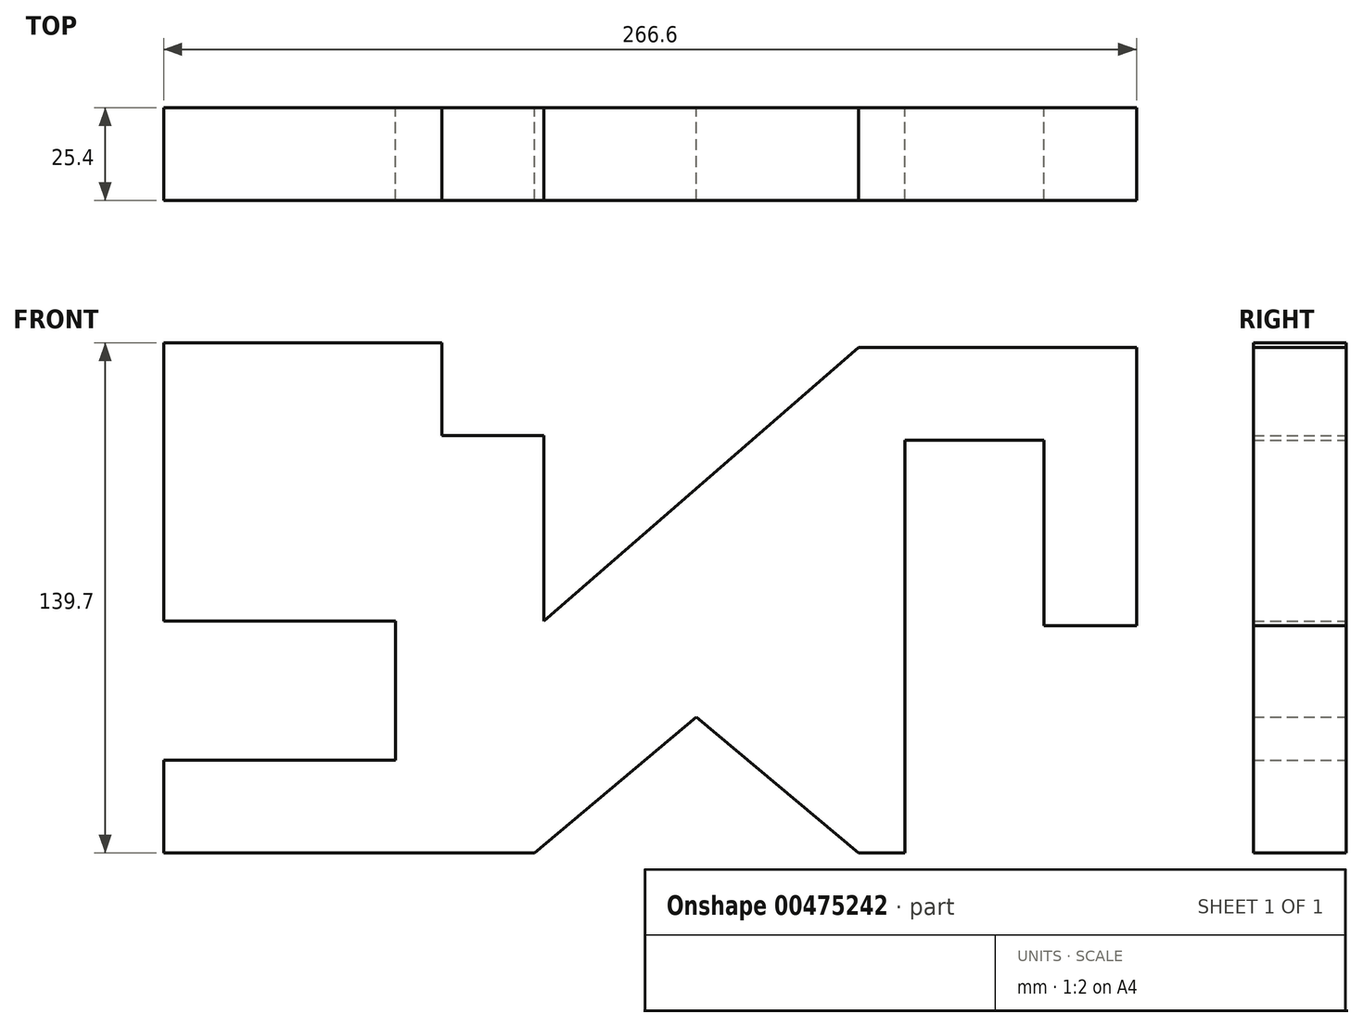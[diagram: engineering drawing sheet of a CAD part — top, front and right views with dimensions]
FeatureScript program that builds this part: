
annotation { "Feature Type Name" : "Feature", "Feature Type Description" : "" }
export const myFeature = defineFeature(function(context is Context, id is Id, definition is map)
    precondition{}
    {
        {
            var Q0;
            Q0=qCreatedBy(makeId("Front.planeOp"),FACE);
            var sketch = newSketch(context, id + "F0", { "sketchPlane" : qUnion([Q0])});
            skLineSegment(sketch, "E0", {"start": v(0, 0) * mm, "end": v(0, 76.2) * mm});
            skLineSegment(sketch, "E1", {"start": v(0, 76.2) * mm, "end": v(76.2, 76.2) * mm});
            skLineSegment(sketch, "E2", {"start": v(76.2, 76.2) * mm, "end": v(76.2, 50.8) * mm});
            skLineSegment(sketch, "E3", {"start": v(76.2, 50.8) * mm, "end": v(104.14, 50.8) * mm});
            skLineSegment(sketch, "E4", {"start": v(104.14, 50.8) * mm, "end": v(104.14, 0) * mm});
            skLineSegment(sketch, "E5", {"start": v(104.14, 0) * mm, "end": v(190.4, 74.99) * mm});
            skLineSegment(sketch, "E6", {"start": v(0, 0) * mm, "end": v(63.5, 0) * mm});
            skLineSegment(sketch, "E7", {"start": v(63.5, 0) * mm, "end": v(63.5, -38.1) * mm});
            skLineSegment(sketch, "E8", {"start": v(63.5, -38.1) * mm, "end": v(0, -38.1) * mm});
            skLineSegment(sketch, "E9", {"start": v(0, -38.1) * mm, "end": v(0, -63.5) * mm});
            skLineSegment(sketch, "E10", {"start": v(0, -63.5) * mm, "end": v(101.6, -63.5) * mm});
            skLineSegment(sketch, "E11", {"start": v(101.6, -63.5) * mm, "end": v(146, -26.24) * mm});
            skLineSegment(sketch, "E12", {"start": v(146, -26.24) * mm, "end": v(190.4, -63.5) * mm});
            skLineSegment(sketch, "E13", {"start": v(190.4, -63.5) * mm, "end": v(203.1, -63.5) * mm});
            skLineSegment(sketch, "E14", {"start": v(190.4, 74.99) * mm, "end": v(266.6, 74.99) * mm});
            skLineSegment(sketch, "E15", {"start": v(266.6, 74.99) * mm, "end": v(266.6, -1.21) * mm});
            skLineSegment(sketch, "E16", {"start": v(266.6, -1.21) * mm, "end": v(241.2, -1.21) * mm});
            skLineSegment(sketch, "E17", {"start": v(241.2, -1.21) * mm, "end": v(241.2, 49.59) * mm});
            skLineSegment(sketch, "E18", {"start": v(203.1, -63.5) * mm, "end": v(203.1, 49.59) * mm});
            skLineSegment(sketch, "E19", {"start": v(241.2, 49.59) * mm, "end": v(203.1, 49.59) * mm});
            skSolve(sketch);
        }
        {
            var Q0;
            Q0 = qSketchRegion(id + "F0", true);
            extrude(context, id + "F1", {"entities" : qUnion([Q0]), "depth" : 25.4 * mm});
        }
    });
